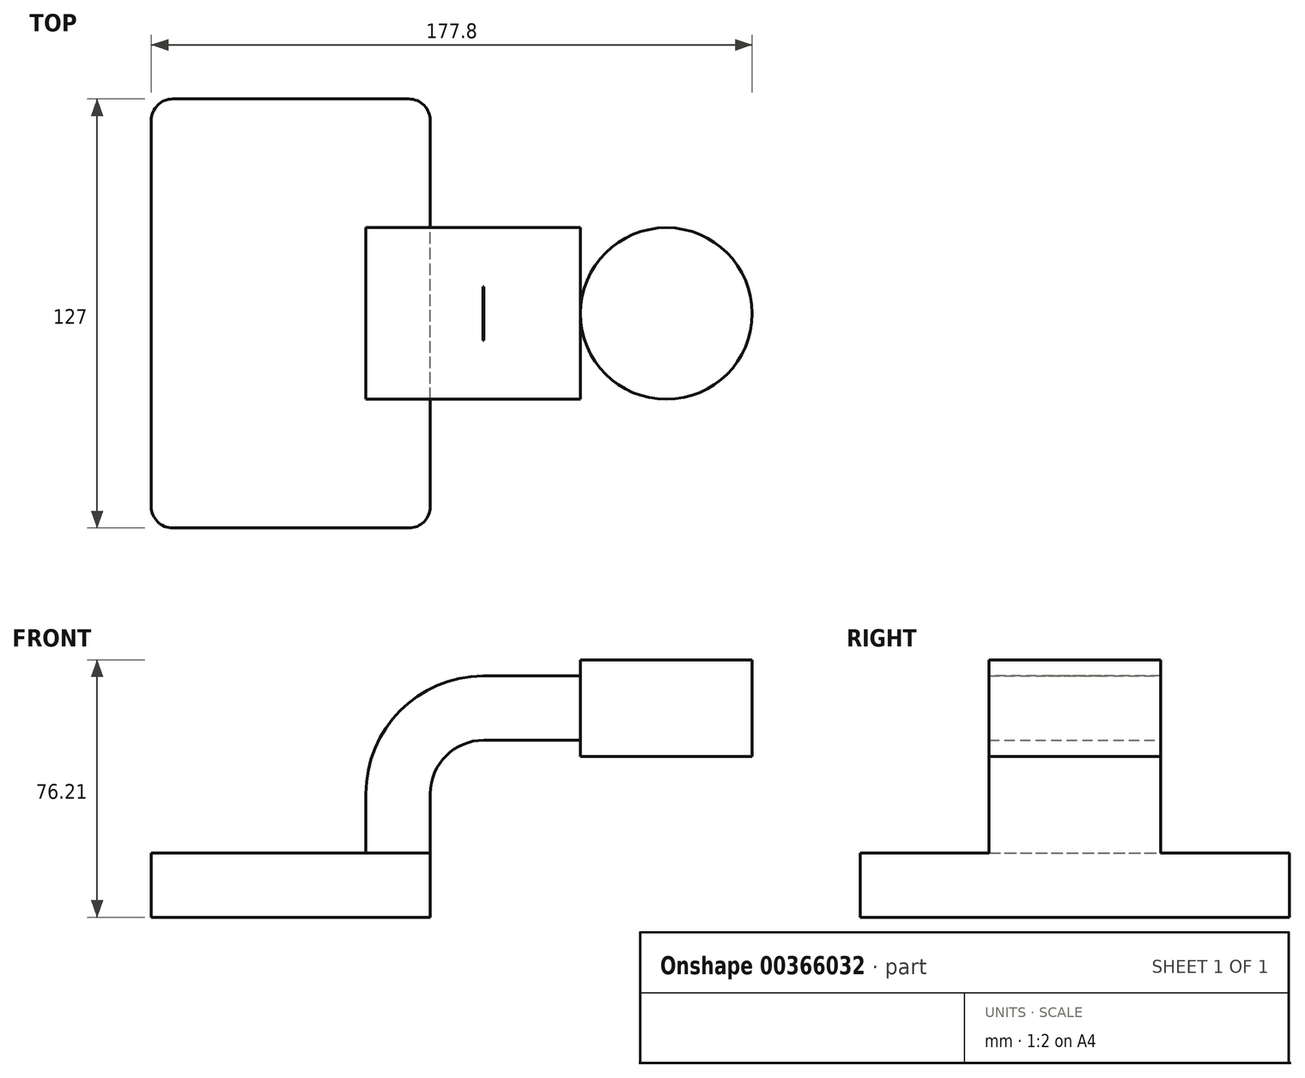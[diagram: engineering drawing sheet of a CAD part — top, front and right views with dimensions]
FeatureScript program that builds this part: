
annotation { "Feature Type Name" : "Feature", "Feature Type Description" : "" }
export const myFeature = defineFeature(function(context is Context, id is Id, definition is map)
    precondition{}
    {
        {
            var Q0;
            Q0=qCreatedBy(makeId("Front.planeOp"),FACE);
            var sketch = newSketch(context, id + "F0", { "sketchPlane" : qUnion([Q0])});
            skPoint(sketch, "E0.middle", {"position": v(0, 0) * mm});
            skLineSegment(sketch, "E1.bottom", {"start": v(-41.28, -9.53) * mm, "end": v(41.28, -9.53) * mm});
            skLineSegment(sketch, "E1.top", {"start": v(-41.28, 9.53) * mm, "end": v(41.28, 9.53) * mm});
            skLineSegment(sketch, "E1.left", {"start": v(-41.28, -9.53) * mm, "end": v(-41.28, 9.53) * mm});
            skLineSegment(sketch, "E1.right", {"start": v(41.28, -9.53) * mm, "end": v(41.28, 9.53) * mm});
            skLineSegment(sketch, "E2.bottom", {"start": v(111.13, 38.1) * mm, "end": v(60.33, 38.1) * mm});
            skLineSegment(sketch, "E2.top", {"start": v(111.13, 66.68) * mm, "end": v(60.33, 66.68) * mm});
            skLineSegment(sketch, "E2.left", {"start": v(111.13, 38.1) * mm, "end": v(111.13, 66.68) * mm});
            skLineSegment(sketch, "E2.right", {"start": v(60.33, 38.1) * mm, "end": v(60.33, 66.68) * mm});
            skPoint(sketch, "E2.middle", {"position": v(85.72, 52.39) * mm});
            skLineSegment(sketch, "E3", {"start": v(41.27, 9.53) * mm, "end": v(41.27, 27) * mm});
            skArc(sketch, "E4", {"start": v(41.27, 27) * mm, "mid": v(45.92, 38.23) * mm, "end": v(57.15, 42.88) * mm});
            skLineSegment(sketch, "E5", {"start": v(57.15, 42.88) * mm, "end": v(85.73, 42.88) * mm});
            skLineSegment(sketch, "E6.0", {"start": v(57.15, 61.93) * mm, "end": v(85.73, 61.93) * mm});
            skArc(sketch, "E6.1", {"start": v(22.23, 27) * mm, "mid": v(32.45, 51.7) * mm, "end": v(57.15, 61.93) * mm});
            skLineSegment(sketch, "E6.2", {"start": v(22.22, 9.53) * mm, "end": v(22.22, 27) * mm});
            skLineSegment(sketch, "E7", {"start": v(85.73, 35.98) * mm, "end": v(85.73, 66.68) * mm});
            skPoint(sketch, "E7.startSnap0", {"position": v(85.73, 38.1) * mm});
            skFitSpline(sketch, "E8", {"points": [v(-41.28, 9.53) * mm, v(57.15, 61.93) * mm], "startDerivative": vector(1.17, 66.03) * mm, "endDerivative": vector(171.45, 0.55) * mm});
            skSolve(sketch);
        }
        {
            var Q0;
            Q0=makeQuery(id+"F0.imprint","IMPRINT",FACE,{"disambiguationData":[TD([[makeQuery(id+"F0.imprint","IMPRINT",EDGE,{"derivedFrom":sQuery(id+"F0.wireOp",EDGE,"E1.bottom")}),1.0]])]});
            extrude(context, id + "F1", {"entities" : qUnion([Q0]), "endBound" : BoundingType.SYMMETRIC, "depth" : 127 * mm});
        }
        {
            var Q0;
            {var subQ5=sQuery(id+"F0.wireOp",EDGE,"E3");Q0=makeQuery(id+"F0.imprint","IMPRINT",FACE,{"disambiguationData":[TD([[makeQuery(id+"F0.imprint","IMPRINT",EDGE,{"derivedFrom":subQ5}),1.0]])]});}
            var Q1;
            {var subQ0=sQuery(id+"F0.wireOp",EDGE,"E5");var subQ1=sQuery(id+"F0.wireOp",EDGE,"E2.right");var subQ2=makeQuery(id+"F0.imprint","INTERSECT",VERTEX,{"derivedFrom":[subQ1,subQ0]});Q1=makeQuery(id+"F0.imprint","IMPRINT",FACE,{"disambiguationData":[TD([[makeQuery(id+"F0.imprint","IMPRINT",EDGE,{"disambiguationData":[TD([[subQ2,-1.0]])],"derivedFrom":subQ1}),-1.0]])]});}
            extrude(context, id + "F2", {"entities" : qUnion([Q0, Q1]), "operationType" : NewBodyOperationType.ADD, "endBound" : BoundingType.SYMMETRIC, "depth" : 50.8 * mm});
        }
        {
            var Q0;
            {var subQ4=sQuery(id+"F0.wireOp",EDGE,"E6.1");Q0=makeQuery(id+"F0.imprint","IMPRINT",FACE,{"disambiguationData":[TD([[makeQuery(id+"F0.imprint","IMPRINT",EDGE,{"derivedFrom":subQ4}),1.0]])]});}
            extrude(context, id + "F3", {"entities" : qUnion([Q0]), "endBound" : BoundingType.SYMMETRIC, "depth" : 15.88 * mm});
        }
        {
            var Q0;
            {var subQ4=sQuery(id+"F0.wireOp",EDGE,"E2.left");Q0=makeQuery(id+"F0.imprint","IMPRINT",FACE,{"disambiguationData":[TD([[makeQuery(id+"F0.imprint","IMPRINT",EDGE,{"derivedFrom":subQ4}),1.0]])]});}
            var Q1;
            Q1=sQuery(id+"F0.wireOp",EDGE,"E2.left");
            revolve(context, id + "F4", {"operationType" : NewBodyOperationType.ADD, "entities" : qUnion([Q0]), "axis" : qUnion([Q1]), "revolveType" : RevolveType.FULL});
        }
        {
            var Q0;
            Q0=makeQuery(id+"F1.opExtrude","CAP_EDGE",EDGE,{"disambiguationData":[OSD([sQuery(id+"F0.wireOp",EDGE,"E1.right")])],"isStart":false});
            var Q1;
            Q1=makeQuery(id+"F1.opExtrude","CAP_EDGE",EDGE,{"disambiguationData":[OSD([sQuery(id+"F0.wireOp",EDGE,"E1.left")])],"isStart":false});
            var Q2;
            Q2=makeQuery(id+"F1.opExtrude","CAP_EDGE",EDGE,{"disambiguationData":[OSD([sQuery(id+"F0.wireOp",EDGE,"E1.right")])],"isStart":true});
            var Q3;
            Q3=makeQuery(id+"F1.opExtrude","CAP_EDGE",EDGE,{"disambiguationData":[OSD([sQuery(id+"F0.wireOp",EDGE,"E1.left")])],"isStart":true});
            fillet(context, id + "F5", {"entities" : qUnion([Q0, Q1, Q2, Q3]), "radius" : 6.35 * mm, "tangentPropagation" : true, "allowEdgeOverflow" : false});
        }
    });
